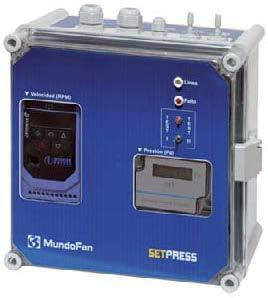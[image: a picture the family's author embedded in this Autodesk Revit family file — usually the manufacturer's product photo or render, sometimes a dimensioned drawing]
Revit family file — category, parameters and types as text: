
# Revit family: SETPRESS-11_VE10812
name_source: partatom
category: Aparatos eléctricos
revit_build: Autodesk Revit 2016 (Build: 20150220_1215(x64)
units: mm (PartAtom-declared; Revit-internal decimal feet)

## family parameters
Compartido = No
Corte con vacíos al cargar = No
Cota de conector redondo = Diámetro de uso
Mantener orientación de anotación = No
Número OmniClass = 23.80.00.00
Punto de cálculo de habitación = No
Se basa en plano de trabajo = No
Siempre vertical = Sí
Tipo de pieza = Caja de conexiones
Título OmniClass = Electric Power and Lighting

## types (1)
- SETPRESS
    Alimentación = 230Vac monofásico
    Corriente = 10,5 A
    Costo = 0 $
    Código de montaje = VE10812
    Descripción = CONTROL EFICIENCIA ENERGETICA PARA VENTILADORES
    Dimensiones máx. = 270x300x170 mm
    Fabricante = SALVADOR ESCODA
    Imagen de tipo = setpress.jpg
    Leds = linea / fallo
    Modelo = SETPRESS 1,1kW
    Normativas = UNE-EN 12101-6
    Potencia = 1,1 kW
    Regulación = Mediante sonda analógica de presión
    Salida = 230Vac monofásico
    URL = www.salvadorescoda.com
    Visualización = frecuencia (Hz) y presión (Pa)
